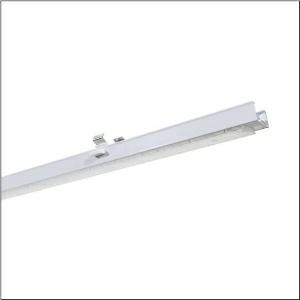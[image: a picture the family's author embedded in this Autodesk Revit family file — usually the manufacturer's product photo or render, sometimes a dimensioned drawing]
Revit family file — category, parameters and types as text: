
# Revit family: sanierungs-leuchteneinsatz_31_gen_2_51re12mb18b_962a
name_source: partatom
category: Lighting Fixtures
units: mm (PartAtom-declared; Revit-internal decimal feet)

## family parameters
Cut with Voids When Loaded = No
Host = Face
Light Source = No
Part Type = Normal
Room Calculation Point = No
Round Connector Dimension = Use Diameter
Shared = No

## types (1)
- --- (1 x LED, 8000 lm, 50 W, 3500K)
    Apparent Load = 50 VA
    CIE Flux Codes = 65 91 98 99 100
    Color Rendering = 80
    Color Temperature = 3500K
    Default Elevation = 1800 mm
    Description = Refurbishment luminaire insert Gen.2, luminaire insert, of extruded aluminium section, coated, traffic white (RAL 9016), length: 1.472mm, width: 91mm, height: 53mm, LED rated luminous flux: 8.000lm, light colour: 835, control gear: ON/OFF Multilumen, control gear: ECG Multilumen, with system connector: socket, mains connection: 220..240V, AC/DC, 0/50..60Hz, luminous flux adjustable on luminaire in four steps (4280/5650/6950/8270lm), connected load according to luminous flux setting (24/32/40/49W), primary light control with lens, of plastic, primary optical cover: cover, of PMMA, light emission: direct distribution, protection rating (complete): IP20, insulation class (complete): insulation class I (protective earthing), certification: CE, UKCA, permissible ambient temperature for indoor applications: -20..+40°C, packaging unit: 1 piece
    Height = 58 mm
    Lamp = 1 x LED
    Lamp Light Flux = 8000 lm
    Lamp Power = 50 W
    Lamp count = 1
    Length = 1472 mm
    Luminous efficacy = 160 lm/W
    Manufacturer = Siteco
    ModVariant = No
    Model = 51RE12MB18B
    Mounting Place = Ceiling
    Mounting Type = Pendant
    Number of Poles = 1
    OnlyDefault = Yes
    Power Factor = 1
    Product Name = Sanierungs-Leuchteneinsatz 31 Gen.2
    Product group = luminaire insert
    ProductGroupID = 902
    Protection Class = Protection class I
    Protection Degree = IP 20
    RLX_Detail_Level = 1
    RlxData = <blob elided: 20309 chars, md5=d6f0b009>
    Socket = socket
    Standby Power = 0 W
    System Light Flux = 8000 lm
    System Power = 50 W
    Type Comments = factory setting: luminous flux: 100 % | (ON | ON) | 300 mA
    Type Image = l_1266702.jpg
    URL = http://relux.com
    VarID = @adj_090909
    Voltage = 0 V
    Weight = 0.00 kg
    Width = 65 mm

## geometry (parser evidence)
native form markers: Blend x4, Sweep x11
no freeform markers — native parametric forms only
